AUTODESK INVENTOR PART (.ipt)
format: ipt  version: 2016 (Build 200138000, 138)  size: 8,490,496 bytes
history: native  units: in
note: dims shown in document units (in); Inventor stores cm internally (conversion verified against a paired STEP export)
features: other x44, sketch x6
ambient origin geometry x8: Origin, YZ Plane, XZ Plane, XY Plane, X Axis, Y Axis, Z Axis, Center Point
bodies: Solid1 (feature_tree)
feature tree (50):
  other  "WheelAssembly.iam"
  other  "am-2648_4inWheel8mmHub.ipt:2"
  other  "545556.ipt:2"
  other  "634080.ipt:1"
  other  "615102.ipt:3"
  other  "615102.ipt:4"
  other  "634080.ipt:2"
  other  "am-2648_4inWheel8mmHub.ipt:3"
  other  "545556.ipt:6"
  other  "615102.ipt:5"
  other  "634080.ipt:3"
  other  "am-2964NeveRest.ipt:2"
  other  "545556.ipt:8"
  other  "615114.ipt:2"
  other  "615114.ipt:3"
  other  "545556.ipt:9"
  other  "am-2964NeveRest.ipt:3"
  other  "Tetrex 2pc motor mount.ipt:1"
  other  "Tetrex 2pc motor mount.ipt:2"
  other  "DriveTrainPlate.iam:1"
  other  "DriveTrainPlate.iam:1::DriveTrainPlate.ipt:1"
  other  "DriveTrainPlate.iam:2"
  other  "DriveTrainPlate.iam:2::DriveTrainPlate.ipt:1"
  other  "545556.ipt:10"
  other  "545456.ipt:1"
  other  "545456.ipt:2"
  other  "545456.ipt:3"
  other  "545556.ipt:11"
  other  "Srf1"
  other  "Srf2"
  other  "Srf3"
  other  "Srf4"
  other  "Srf5"
  other  "Srf6"
  other  "Srf7"
  other  "Srf8"
  sketch  "Sketch 1"  dims[d0=0.3937in]
  sketch  "Sketch 16"
  sketch  "Sketch3"
  sketch  "Sketch 1_1"
  sketch  "Sketch 16_1"
  sketch  "Sketch3_1"
  other  "Solid5::Derived"
  other  "Solid6::Derived"
  other  "Solid7::Derived"
  other  "Solid8::Derived"
  other  "Solid5::Derived_1"
  other  "Solid6::Derived_1"
  other  "Solid7::Derived_1"
  other  "Solid8::Derived_1"
